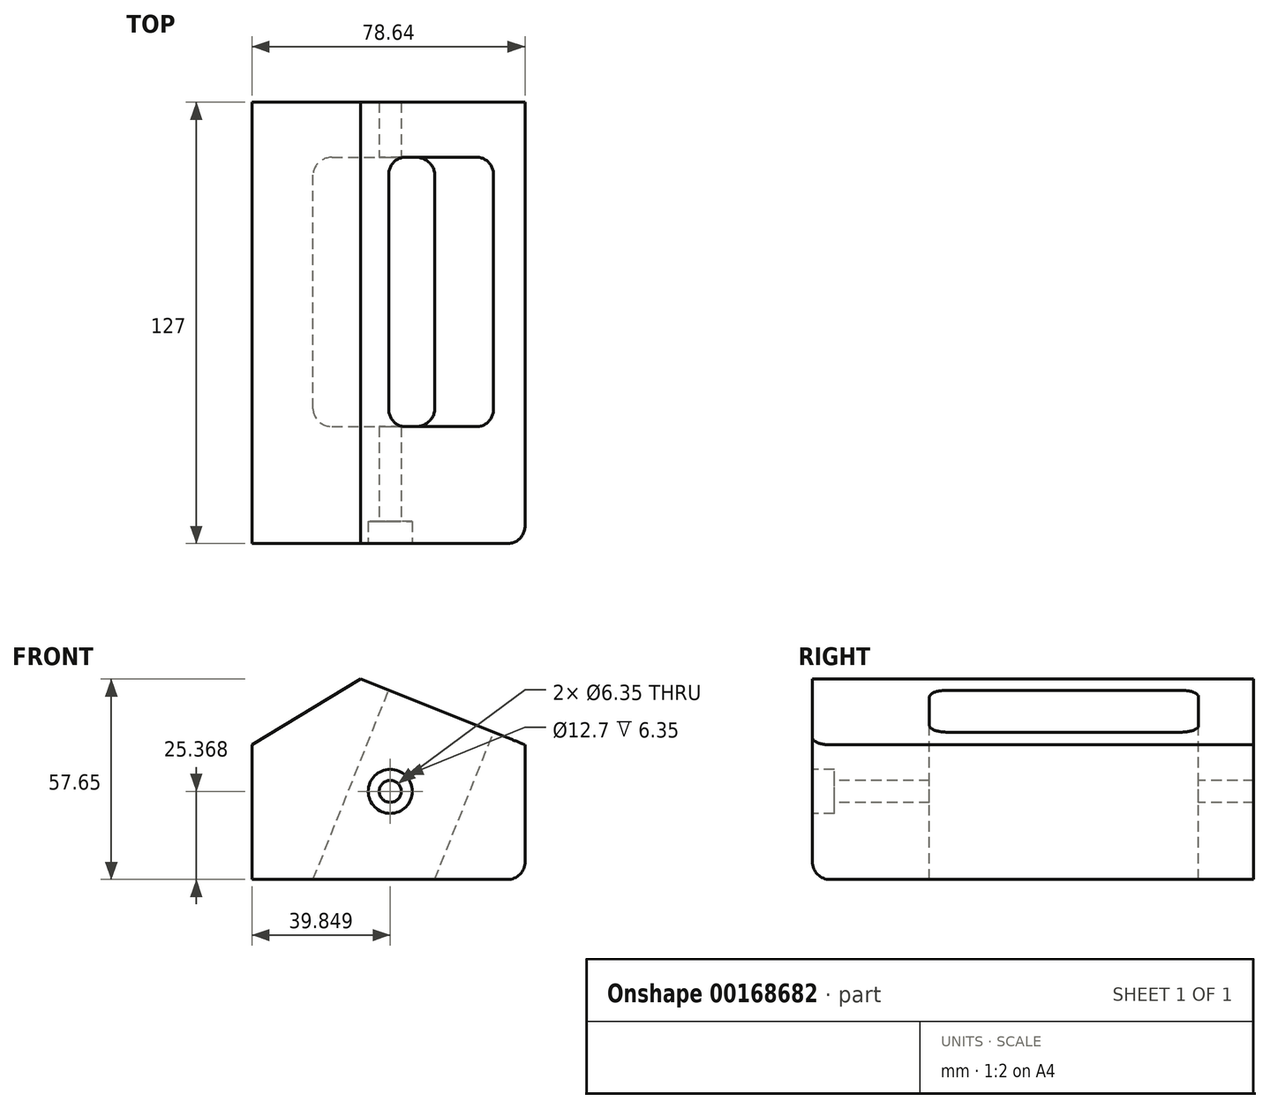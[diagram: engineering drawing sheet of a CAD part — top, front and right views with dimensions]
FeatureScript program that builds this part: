
annotation { "Feature Type Name" : "Feature", "Feature Type Description" : "" }
export const myFeature = defineFeature(function(context is Context, id is Id, definition is map)
    precondition{}
    {
        {
            var Q0;
            Q0=qCreatedBy(makeId("Front.planeOp"),FACE);
            var sketch = newSketch(context, id + "F0", { "sketchPlane" : qUnion([Q0])});
            skLineSegment(sketch, "E0.bottom", {"start": v(-60.86, 0) * mm, "end": v(17.78, 0) * mm});
            skLineSegment(sketch, "E0.left", {"start": v(-60.86, 0) * mm, "end": v(-60.86, 38.77) * mm});
            skLineSegment(sketch, "E0.right", {"start": v(17.78, 0) * mm, "end": v(17.78, 38.77) * mm});
            skLineSegment(sketch, "E1", {"start": v(-29.51, 57.65) * mm, "end": v(17.78, 38.77) * mm});
            skLineSegment(sketch, "E2", {"start": v(-29.51, 57.65) * mm, "end": v(-60.86, 38.77) * mm});
            skSolve(sketch);
        }
        {
            var Q0;
            Q0=makeQuery(id+"F0.imprint","IMPRINT",FACE,{"disambiguationData":[TD([[makeQuery(id+"F0.imprint","IMPRINT",EDGE,{"derivedFrom":sQuery(id+"F0.wireOp",EDGE,"E0.bottom")}),1.0]])]});
            extrude(context, id + "F1", {"entities" : qUnion([Q0]), "depth" : 127 * mm});
        }
        {
            var Q0;
            Q0=makeQuery(id+"F1.opExtrude","CAP_FACE",FACE,{"disambiguationData":[OSD([sQuery(id+"F0.wireOp",EDGE,"E0.bottom"),sQuery(id+"F0.wireOp",EDGE,"E0.left"),sQuery(id+"F0.wireOp",EDGE,"E0.right"),sQuery(id+"F0.wireOp",EDGE,"E1"),sQuery(id+"F0.wireOp",EDGE,"E2")])],"isStart":false});
            var sketch = newSketch(context, id + "F2", { "sketchPlane" : qUnion([Q0])});
            skPoint(sketch, "E3", {"position": v(-30.7, 27.67) * mm});
            skPoint(sketch, "E4", {"position": v(-21.01, 25.37) * mm});
            skSolve(sketch);
        }
        {
            var Q0;
            Q0=sQuery(id+"F2.wireOp",VERTEX,"E4");
            var Q1;
            Q1=makeQuery(id+"F1.opExtrude","SWEPT_BODY",BODY,{"disambiguationData":[OSD([sQuery(id+"F0.wireOp",EDGE,"E0.bottom"),sQuery(id+"F0.wireOp",EDGE,"E0.left"),sQuery(id+"F0.wireOp",EDGE,"E0.right"),sQuery(id+"F0.wireOp",EDGE,"E1"),sQuery(id+"F0.wireOp",EDGE,"E2")])]});
            hole(context, id + "F3", {"style" : HoleStyle.C_BORE, "endStyle" : HoleEndStyle.THROUGH, "holeDiameter" : 6.35 * mm, "cBoreDiameter" : 12.7 * mm, "cBoreDepth" : 6.35 * mm, "locations" : qUnion([Q0]), "scope" : qUnion([Q1]), "isTappedThrough" : true});
        }
        {
            var Q0;
            Q0=makeQuery(id+"F1.opExtrude","CAP_EDGE",EDGE,{"disambiguationData":[OSD([sQuery(id+"F0.wireOp",EDGE,"E0.bottom")])],"isStart":false});
            var Q1;
            Q1=makeQuery(id+"F1.opExtrude","CAP_EDGE",EDGE,{"disambiguationData":[OSD([sQuery(id+"F0.wireOp",EDGE,"E0.right")])],"isStart":false});
            var Q2;
            Q2=makeQuery(id+"F1.opExtrude","SWEPT_EDGE",EDGE,{"disambiguationData":[OSD([sQuery(id+"F0.wireOp",EDGE,"E0.bottom"),sQuery(id+"F0.wireOp",EDGE,"E0.right")])]});
            fillet(context, id + "F4", {"entities" : qUnion([Q0, Q1, Q2]), "radius" : 5.08 * mm, "tangentPropagation" : true, "allowEdgeOverflow" : false});
        }
        {
            var Q0;
            Q0=makeQuery(id+"F1.opExtrude","SWEPT_FACE",FACE,{"disambiguationData":[OSD([sQuery(id+"F0.wireOp",EDGE,"E1")])]});
            var sketch = newSketch(context, id + "F5", { "sketchPlane" : qUnion([Q0])});
            skLineSegment(sketch, "E5.bottom", {"start": v(-40.15, -93.3) * mm, "end": v(-7.63, -93.3) * mm});
            skLineSegment(sketch, "E5.top", {"start": v(-40.15, -15.84) * mm, "end": v(-7.63, -15.84) * mm});
            skLineSegment(sketch, "E5.left", {"start": v(-40.15, -93.3) * mm, "end": v(-40.15, -15.84) * mm});
            skLineSegment(sketch, "E5.right", {"start": v(-7.63, -93.3) * mm, "end": v(-7.63, -15.84) * mm});
            skSolve(sketch);
        }
        {
            var Q0;
            Q0=makeQuery(id+"F5.imprint","IMPRINT",FACE,{"disambiguationData":[TD([[makeQuery(id+"F5.imprint","IMPRINT",EDGE,{"derivedFrom":sQuery(id+"F5.wireOp",EDGE,"E5.bottom")}),1.0]])]});
            extrude(context, id + "F6", {"entities" : qUnion([Q0]), "operationType" : NewBodyOperationType.REMOVE, "endBound" : BoundingType.THROUGH_ALL, "oppositeDirection" : true, "depth" : 25.4 * mm});
        }
        {
            var Q0;
            Q0=makeQuery(id+"F6.boolean.opBoolean","COPY",EDGE,{"derivedFrom":makeQuery(id+"F6.opExtrude","SWEPT_EDGE",EDGE,{"disambiguationData":[OSD([sQuery(id+"F5.wireOp",EDGE,"E5.top"),sQuery(id+"F5.wireOp",EDGE,"E5.left")])]})});
            var Q1;
            Q1=makeQuery(id+"F6.boolean.opBoolean","COPY",EDGE,{"derivedFrom":makeQuery(id+"F6.opExtrude","SWEPT_EDGE",EDGE,{"disambiguationData":[OSD([sQuery(id+"F5.wireOp",EDGE,"E5.top"),sQuery(id+"F5.wireOp",EDGE,"E5.right")])]})});
            var Q2;
            Q2=makeQuery(id+"F6.boolean.opBoolean","COPY",EDGE,{"derivedFrom":makeQuery(id+"F6.opExtrude","SWEPT_EDGE",EDGE,{"disambiguationData":[OSD([sQuery(id+"F5.wireOp",EDGE,"E5.bottom"),sQuery(id+"F5.wireOp",EDGE,"E5.right")])]})});
            var Q3;
            Q3=makeQuery(id+"F6.boolean.opBoolean","COPY",EDGE,{"derivedFrom":makeQuery(id+"F6.opExtrude","SWEPT_EDGE",EDGE,{"disambiguationData":[OSD([sQuery(id+"F5.wireOp",EDGE,"E5.bottom"),sQuery(id+"F5.wireOp",EDGE,"E5.left")])]})});
            fillet(context, id + "F7", {"entities" : qUnion([Q0, Q1, Q2, Q3]), "radius" : 5.08 * mm, "tangentPropagation" : true, "allowEdgeOverflow" : false});
        }
    });
